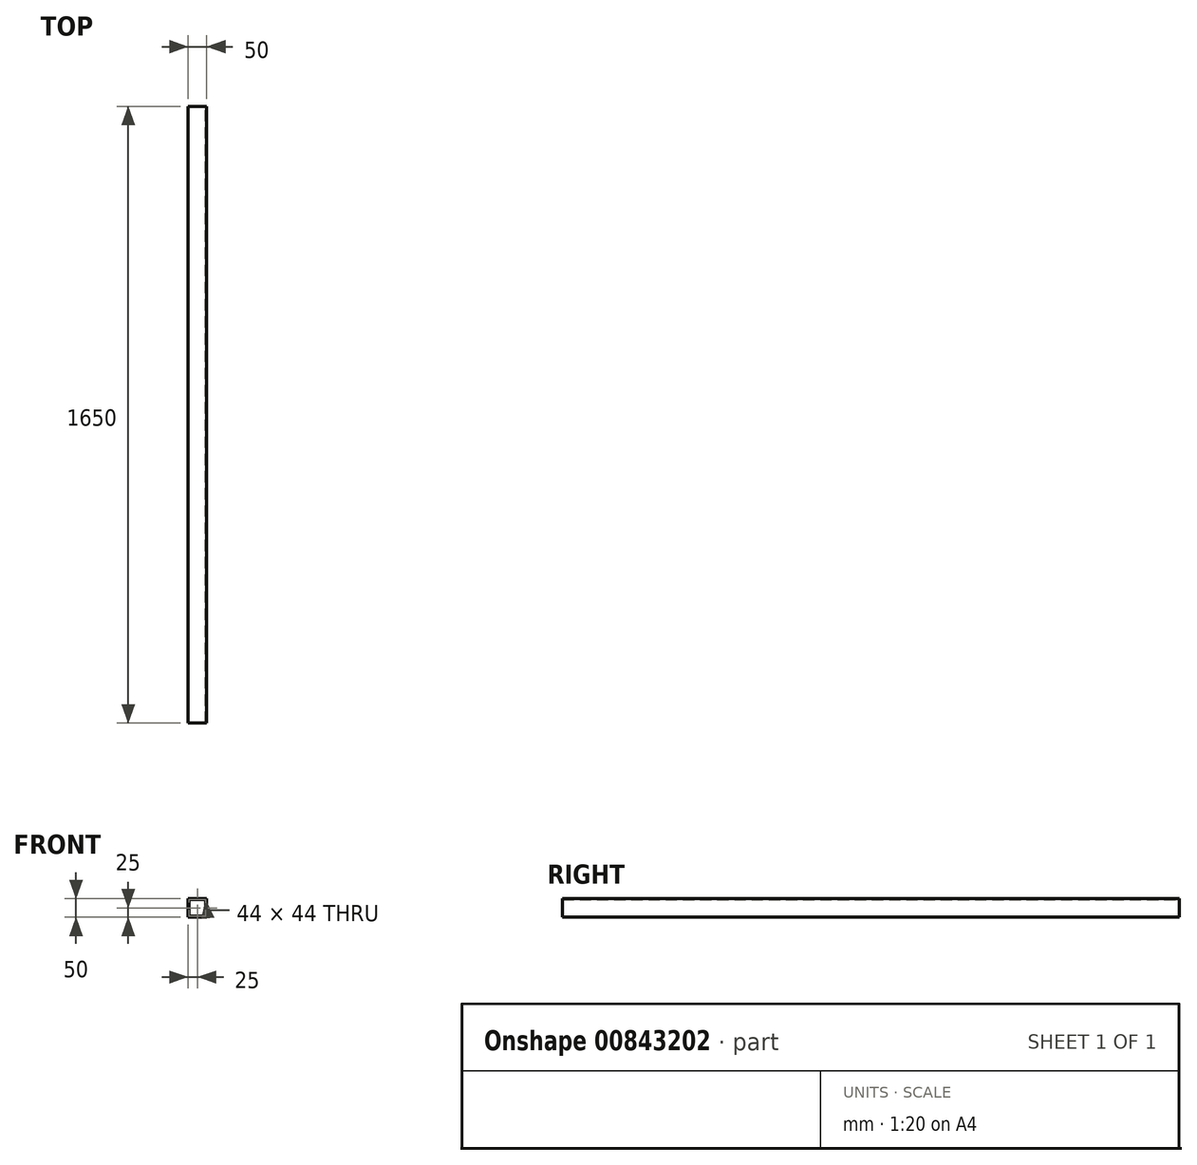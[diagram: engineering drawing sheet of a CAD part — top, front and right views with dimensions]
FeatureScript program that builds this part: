
annotation { "Feature Type Name" : "Feature", "Feature Type Description" : "" }
export const myFeature = defineFeature(function(context is Context, id is Id, definition is map)
    precondition{}
    {
        {
            var Q0;
            Q0=qCreatedBy(makeId("Front.planeOp"),FACE);
            var sketch = newSketch(context, id + "F0", { "sketchPlane" : qUnion([Q0])});
            skLineSegment(sketch, "E0.bottom", {"start": v(25, -25) * mm, "end": v(-25, -25) * mm});
            skLineSegment(sketch, "E0.top", {"start": v(25, 25) * mm, "end": v(-25, 25) * mm});
            skLineSegment(sketch, "E0.left", {"start": v(25, -25) * mm, "end": v(25, 25) * mm});
            skLineSegment(sketch, "E0.right", {"start": v(-25, -25) * mm, "end": v(-25, 25) * mm});
            skPoint(sketch, "E0.middle", {"position": v(0, 0) * mm});
            skLineSegment(sketch, "E1.0", {"start": v(22, 22) * mm, "end": v(-22, 22) * mm});
            skLineSegment(sketch, "E1.1", {"start": v(22, -22) * mm, "end": v(22, 22) * mm});
            skLineSegment(sketch, "E1.2", {"start": v(22, -22) * mm, "end": v(-22, -22) * mm});
            skLineSegment(sketch, "E1.3", {"start": v(-22, -22) * mm, "end": v(-22, 22) * mm});
            skSolve(sketch);
        }
        {
            var Q0;
            Q0=makeQuery(id+"F0.imprint","IMPRINT",FACE,{"disambiguationData":[TD([[makeQuery(id+"F0.imprint","IMPRINT",EDGE,{"derivedFrom":sQuery(id+"F0.wireOp",EDGE,"E0.bottom")}),-1.0]])]});
            extrude(context, id + "F1", {"entities" : qUnion([Q0]), "depth" : 1650 * mm, "offsetDistance" : 25 * mm});
        }
    });
